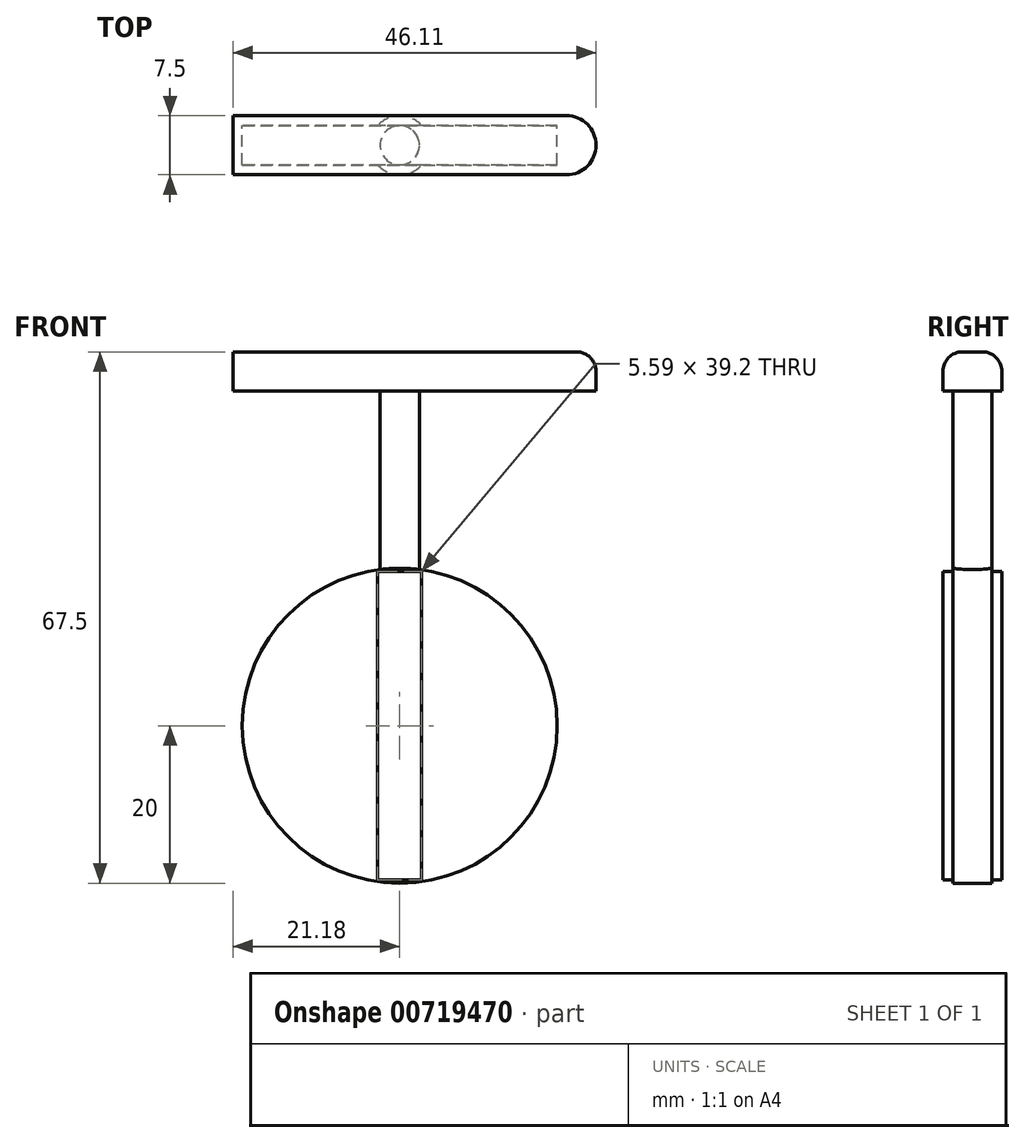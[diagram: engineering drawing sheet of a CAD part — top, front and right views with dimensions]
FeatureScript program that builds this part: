
annotation { "Feature Type Name" : "Feature", "Feature Type Description" : "" }
export const myFeature = defineFeature(function(context is Context, id is Id, definition is map)
    precondition{}
    {
        {
            var Q0;
            Q0=qCreatedBy(makeId("Front.planeOp"),FACE);
            var sketch = newSketch(context, id + "F0", { "sketchPlane" : qUnion([Q0])});
            skCircle(sketch, "E0", {"center": v(0, 0) * mm, "radius": 20 * mm});
            skSolve(sketch);
        }
        {
            var Q0;
            Q0=makeQuery(id+"F0.imprint","IMPRINT",FACE,{"disambiguationData":[TD([[makeQuery(id+"F0.imprint","IMPRINT",EDGE,{"derivedFrom":sQuery(id+"F0.wireOp",EDGE,"E0")}),1.0]])]});
            extrude(context, id + "F1", {"entities" : qUnion([Q0]), "endBound" : BoundingType.SYMMETRIC, "depth" : 5 * mm, "offsetDistance" : 25 * mm});
        }
        {
            var Q0;
            Q0=qCreatedBy(makeId("Top.planeOp"),FACE);
            var sketch = newSketch(context, id + "F2", { "sketchPlane" : qUnion([Q0])});
            skCircle(sketch, "E1", {"center": v(0, 0) * mm, "radius": 2.5 * mm});
            skSolve(sketch);
        }
        {
            var Q0;
            Q0 = qSketchRegion(id + "F2", true);
            extrude(context, id + "F3", {"entities" : qUnion([Q0]), "operationType" : NewBodyOperationType.ADD, "depth" : 42.5 * mm, "offsetDistance" : 25 * mm});
        }
        {
            var Q0;
            Q0=makeQuery(id+"F3.opExtrude","CAP_FACE",FACE,{"disambiguationData":[OSD([sQuery(id+"F2.wireOp",EDGE,"E1")])],"isStart":false});
            var sketch = newSketch(context, id + "F4", { "sketchPlane" : qUnion([Q0])});
            skLineSegment(sketch, "E2.bottom", {"start": v(21.18, 3.75) * mm, "end": v(-21.18, 3.75) * mm});
            skLineSegment(sketch, "E2.top", {"start": v(21.18, -3.75) * mm, "end": v(-21.18, -3.75) * mm});
            skLineSegment(sketch, "E2.left", {"start": v(21.18, 3.75) * mm, "end": v(21.18, -3.75) * mm});
            skPoint(sketch, "E2.middle", {"position": v(0, 0) * mm});
            skArc(sketch, "E3", {"start": v(21.18, -3.75) * mm, "mid": v(24.93, 0) * mm, "end": v(21.18, 3.75) * mm});
            skLineSegment(sketch, "E4", {"start": v(-21.18, -3.75) * mm, "end": v(-21.18, 3.75) * mm});
            skSolve(sketch);
        }
        {
            var Q0;
            Q0 = qSketchRegion(id + "F4", true);
            extrude(context, id + "F5", {"entities" : qUnion([Q0]), "operationType" : NewBodyOperationType.ADD, "depth" : 5 * mm, "offsetDistance" : 25 * mm});
        }
        {
            var Q0;
            Q0=makeQuery(id+"F5.opExtrude","CAP_EDGE",EDGE,{"disambiguationData":[OSD([sQuery(id+"F4.wireOp",EDGE,"E2.bottom")])],"isStart":false});
            var Q1;
            Q1=makeQuery(id+"F5.opExtrude","CAP_EDGE",EDGE,{"disambiguationData":[OSD([sQuery(id+"F4.wireOp",EDGE,"E2.top")])],"isStart":false});
            var Q2;
            Q2=makeQuery(id+"F5.opExtrude","CAP_EDGE",EDGE,{"disambiguationData":[OSD([sQuery(id+"F4.wireOp",EDGE,"E3")])],"isStart":false});
            fillet(context, id + "F6", {"entities" : qUnion([Q0, Q1, Q2]), "radius" : 2.5 * mm, "tangentPropagation" : true, "allowEdgeOverflow" : false});
        }
        {
            var Q0;
            Q0=qCreatedBy(makeId("Top.planeOp"),FACE);
            var sketch = newSketch(context, id + "F7", { "sketchPlane" : qUnion([Q0])});
            skCircle(sketch, "E5", {"center": v(0, 0) * mm, "radius": 3.75 * mm});
            skSolve(sketch);
        }
        {
            var Q0;
            Q0 = qSketchRegion(id + "F7", true);
            extrude(context, id + "F8", {"entities" : qUnion([Q0]), "operationType" : NewBodyOperationType.ADD, "depth" : 19.6 * mm, "offsetDistance" : 25 * mm, "hasSecondDirection" : true, "secondDirectionOppositeDirection" : true, "secondDirectionDepth" : 19.6 * mm});
        }
    });
